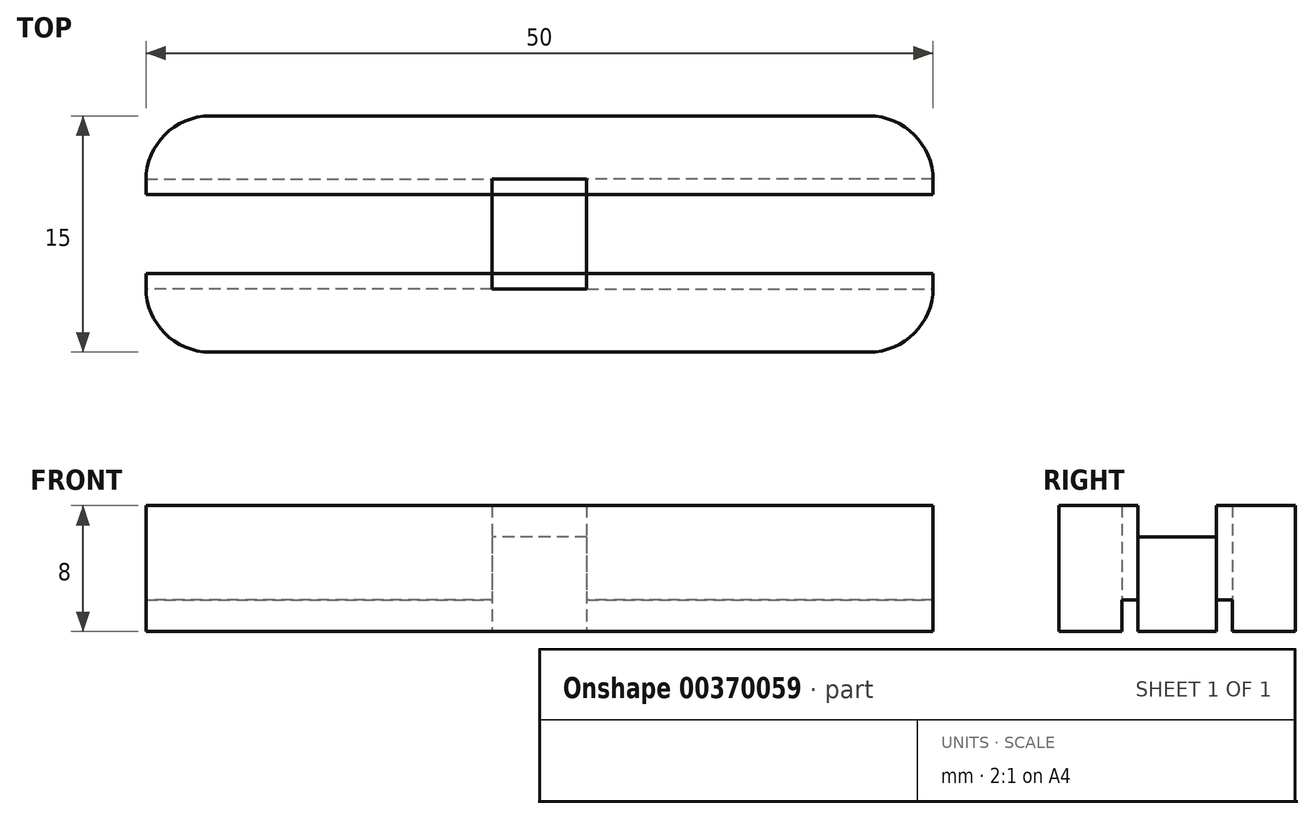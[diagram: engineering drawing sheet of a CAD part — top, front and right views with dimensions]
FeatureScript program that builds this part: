
annotation { "Feature Type Name" : "Feature", "Feature Type Description" : "" }
export const myFeature = defineFeature(function(context is Context, id is Id, definition is map)
    precondition{}
    {
        {
            var Q0;
            Q0=qCreatedBy(makeId("Top.planeOp"),FACE);
            var sketch = newSketch(context, id + "F0", { "sketchPlane" : qUnion([Q0])});
            skLineSegment(sketch, "E0.bottom", {"start": v(25, 7.5) * mm, "end": v(-25, 7.5) * mm});
            skLineSegment(sketch, "E0.top", {"start": v(25, -7.5) * mm, "end": v(-25, -7.5) * mm});
            skLineSegment(sketch, "E0.left", {"start": v(25, 7.5) * mm, "end": v(25, -7.5) * mm});
            skLineSegment(sketch, "E0.right", {"start": v(-25, 7.5) * mm, "end": v(-25, -7.5) * mm});
            skPoint(sketch, "E0.middle", {"position": v(0, 0) * mm});
            skPoint(sketch, "E1", {"position": v(-12.5, 0) * mm});
            skPoint(sketch, "E2", {"position": v(12.5, 0) * mm});
            skLineSegment(sketch, "E3.bottom", {"start": v(3, 3.5) * mm, "end": v(-3, 3.5) * mm});
            skLineSegment(sketch, "E3.top", {"start": v(3, -3.5) * mm, "end": v(-3, -3.5) * mm});
            skLineSegment(sketch, "E3.left", {"start": v(3, 3.5) * mm, "end": v(3, -3.5) * mm});
            skLineSegment(sketch, "E3.right", {"start": v(-3, 3.5) * mm, "end": v(-3, -3.5) * mm});
            skLineSegment(sketch, "E4.bottom", {"start": v(3, 2.5) * mm, "end": v(-3, 2.5) * mm});
            skLineSegment(sketch, "E4.top", {"start": v(3, -2.5) * mm, "end": v(-3, -2.5) * mm});
            skLineSegment(sketch, "E4.left", {"start": v(3, 2.5) * mm, "end": v(3, -2.5) * mm});
            skLineSegment(sketch, "E4.right", {"start": v(-3, 2.5) * mm, "end": v(-3, -2.5) * mm});
            skLineSegment(sketch, "E5", {"start": v(-3, 2.5) * mm, "end": v(-25, 2.5) * mm});
            skLineSegment(sketch, "E6", {"start": v(-25, 2.5) * mm, "end": v(-25, 3.5) * mm});
            skLineSegment(sketch, "E7", {"start": v(-25, 3.5) * mm, "end": v(-3, 3.5) * mm});
            skLineSegment(sketch, "E8", {"start": v(3, 2.5) * mm, "end": v(25, 2.5) * mm});
            skLineSegment(sketch, "E9", {"start": v(25, 2.5) * mm, "end": v(25, 3.5) * mm});
            skLineSegment(sketch, "E10", {"start": v(25, 3.5) * mm, "end": v(3, 3.5) * mm});
            skLineSegment(sketch, "E11", {"start": v(3, -2.5) * mm, "end": v(25, -2.5) * mm});
            skLineSegment(sketch, "E12", {"start": v(3, -3.5) * mm, "end": v(25, -3.5) * mm});
            skLineSegment(sketch, "E13", {"start": v(25, -3.5) * mm, "end": v(25, -2.5) * mm});
            skLineSegment(sketch, "E14", {"start": v(-3, -3.5) * mm, "end": v(-25, -3.5) * mm});
            skLineSegment(sketch, "E15", {"start": v(-25, -3.5) * mm, "end": v(-25, -2.5) * mm});
            skLineSegment(sketch, "E16", {"start": v(-25, -2.5) * mm, "end": v(-3, -2.5) * mm});
            skSolve(sketch);
        }
        {
            var Q0;
            Q0=makeQuery(id+"F0.imprint","IMPRINT",FACE,{"disambiguationData":[TD([[makeQuery(id+"F0.imprint","IMPRINT",EDGE,{"derivedFrom":sQuery(id+"F0.wireOp",EDGE,"E0.bottom")}),1.0]])]});
            var Q1;
            {var subQ2=sQuery(id+"F0.wireOp",EDGE,"E11");Q1=makeQuery(id+"F0.imprint","IMPRINT",FACE,{"disambiguationData":[TD([[makeQuery(id+"F0.imprint","IMPRINT",EDGE,{"derivedFrom":subQ2}),-1.0]])]});}
            var Q2;
            {var subQ0=sQuery(id+"F0.wireOp",EDGE,"E14");Q2=makeQuery(id+"F0.imprint","IMPRINT",FACE,{"disambiguationData":[TD([[makeQuery(id+"F0.imprint","IMPRINT",EDGE,{"derivedFrom":subQ0}),-1.0]])]});}
            var Q3;
            {var subQ1=sQuery(id+"F0.wireOp",EDGE,"E0.top");Q3=makeQuery(id+"F0.imprint","IMPRINT",FACE,{"disambiguationData":[TD([[makeQuery(id+"F0.imprint","IMPRINT",EDGE,{"derivedFrom":subQ1}),-1.0]])]});}
            var Q4;
            Q4=makeQuery(id+"F0.imprint","IMPRINT",FACE,{"disambiguationData":[TD([[makeQuery(id+"F0.imprint","IMPRINT",EDGE,{"derivedFrom":sQuery(id+"F0.wireOp",EDGE,"E4.right")}),-1.0]])]});
            var Q5;
            Q5=makeQuery(id+"F0.imprint","IMPRINT",FACE,{"disambiguationData":[TD([[makeQuery(id+"F0.imprint","IMPRINT",EDGE,{"derivedFrom":sQuery(id+"F0.wireOp",EDGE,"E4.left")}),1.0]])]});
            var Q6;
            {var subQ2=sQuery(id+"F0.wireOp",EDGE,"E8");Q6=makeQuery(id+"F0.imprint","IMPRINT",FACE,{"disambiguationData":[TD([[makeQuery(id+"F0.imprint","IMPRINT",EDGE,{"derivedFrom":subQ2}),1.0]])]});}
            var Q7;
            {var subQ2=sQuery(id+"F0.wireOp",EDGE,"E5");Q7=makeQuery(id+"F0.imprint","IMPRINT",FACE,{"disambiguationData":[TD([[makeQuery(id+"F0.imprint","IMPRINT",EDGE,{"derivedFrom":subQ2}),-1.0]])]});}
            extrude(context, id + "F1", {"entities" : qUnion([Q0, Q1, Q2, Q3, Q4, Q5, Q6, Q7]), "depth" : 8 * mm, "offsetDistance" : 25.4 * mm});
        }
        {
            var Q0;
            Q0=makeQuery(id+"F0.imprint","IMPRINT",FACE,{"disambiguationData":[TD([[makeQuery(id+"F0.imprint","IMPRINT",EDGE,{"derivedFrom":sQuery(id+"F0.wireOp",EDGE,"E3.bottom")}),1.0]])]});
            extrude(context, id + "F2", {"entities" : qUnion([Q0]), "operationType" : NewBodyOperationType.REMOVE, "depth" : 17.53 * mm, "offsetDistance" : 25.4 * mm});
        }
        {
            var Q0;
            Q0=sQuery(id+"F0.wireOp",VERTEX,"E1");
            var Q1;
            Q1=sQuery(id+"F0.wireOp",VERTEX,"E2");
            var Q2;
            Q2=makeQuery(id+"F1.opExtrude","SWEPT_BODY",BODY,{"disambiguationData":[OSD([sQuery(id+"F0.wireOp",EDGE,"E0.bottom"),sQuery(id+"F0.wireOp",EDGE,"E0.top"),sQuery(id+"F0.wireOp",EDGE,"E0.left"),sQuery(id+"F0.wireOp",EDGE,"E0.right")])]});
            hole(context, id + "F3", {"style" : HoleStyle.SIMPLE, "endStyle" : HoleEndStyle.BLIND, "oppositeDirection" : true, "holeDiameter" : 4.5 * mm, "majorDiameter" : 6.35 * mm, "holeDepth" : 10 * mm, "isTappedThrough" : true, "tappedDepth" : 12.7 * mm, "tapClearance" : 3, "locations" : qUnion([Q0, Q1]), "scope" : qUnion([Q2])});
        }
        {
            var Q0;
            Q0=makeQuery(id+"F0.imprint","IMPRINT",FACE,{"disambiguationData":[TD([[makeQuery(id+"F0.imprint","IMPRINT",EDGE,{"derivedFrom":sQuery(id+"F0.wireOp",EDGE,"E4.bottom")}),1.0]])]});
            extrude(context, id + "F4", {"entities" : qUnion([Q0]), "operationType" : NewBodyOperationType.ADD, "depth" : 6 * mm, "offsetDistance" : 25.4 * mm});
        }
        {
            var Q0;
            {var subQ0=sQuery(id+"F0.wireOp",EDGE,"E14");Q0=makeQuery(id+"F0.imprint","IMPRINT",FACE,{"disambiguationData":[TD([[makeQuery(id+"F0.imprint","IMPRINT",EDGE,{"derivedFrom":subQ0}),-1.0]])]});}
            var Q1;
            {var subQ2=sQuery(id+"F0.wireOp",EDGE,"E11");Q1=makeQuery(id+"F0.imprint","IMPRINT",FACE,{"disambiguationData":[TD([[makeQuery(id+"F0.imprint","IMPRINT",EDGE,{"derivedFrom":subQ2}),-1.0]])]});}
            var Q2;
            {var subQ2=sQuery(id+"F0.wireOp",EDGE,"E8");Q2=makeQuery(id+"F0.imprint","IMPRINT",FACE,{"disambiguationData":[TD([[makeQuery(id+"F0.imprint","IMPRINT",EDGE,{"derivedFrom":subQ2}),1.0]])]});}
            var Q3;
            {var subQ2=sQuery(id+"F0.wireOp",EDGE,"E5");Q3=makeQuery(id+"F0.imprint","IMPRINT",FACE,{"disambiguationData":[TD([[makeQuery(id+"F0.imprint","IMPRINT",EDGE,{"derivedFrom":subQ2}),-1.0]])]});}
            extrude(context, id + "F5", {"entities" : qUnion([Q0, Q1, Q2, Q3]), "operationType" : NewBodyOperationType.REMOVE, "depth" : 2 * mm, "offsetDistance" : 25.4 * mm});
        }
        {
            var Q0;
            Q0=makeQuery(id+"F1.opExtrude","SWEPT_EDGE",EDGE,{"disambiguationData":[OSD([sQuery(id+"F0.wireOp",EDGE,"E0.top"),sQuery(id+"F0.wireOp",EDGE,"E0.left")])]});
            var Q1;
            Q1=makeQuery(id+"F1.opExtrude","SWEPT_EDGE",EDGE,{"disambiguationData":[OSD([sQuery(id+"F0.wireOp",EDGE,"E0.bottom"),sQuery(id+"F0.wireOp",EDGE,"E0.left")])]});
            var Q2;
            Q2=makeQuery(id+"F1.opExtrude","SWEPT_EDGE",EDGE,{"disambiguationData":[OSD([sQuery(id+"F0.wireOp",EDGE,"E0.bottom"),sQuery(id+"F0.wireOp",EDGE,"E0.right")])]});
            var Q3;
            Q3=makeQuery(id+"F1.opExtrude","SWEPT_EDGE",EDGE,{"disambiguationData":[OSD([sQuery(id+"F0.wireOp",EDGE,"E0.top"),sQuery(id+"F0.wireOp",EDGE,"E0.right")])]});
            fillet(context, id + "F6", {"entities" : qUnion([Q0, Q1, Q2, Q3]), "radius" : 4.1 * mm, "tangentPropagation" : true, "allowEdgeOverflow" : false});
        }
    });
